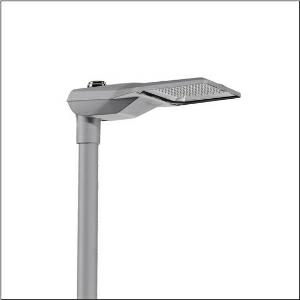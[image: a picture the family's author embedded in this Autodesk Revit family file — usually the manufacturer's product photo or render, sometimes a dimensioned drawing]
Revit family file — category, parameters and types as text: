
# Revit family: streetlight_sl_21_midi___p0_8a_5xe7u57n08mb_b7af
name_source: partatom
category: Lighting Fixtures
units: mm (PartAtom-declared; Revit-internal decimal feet)

## family parameters
Cut with Voids When Loaded = No
Host = Face
Light Source = No
Part Type = Normal
Room Calculation Point = No
Round Connector Dimension = Use Diameter
Shared = No

## types (1)
- --- (1 x LED, 15940 lm, 137 W, 3000K)
    Apparent Load = 137 VA
    CIE Flux Codes = 33 69 96 100 100
    Color Rendering = 80
    Color Temperature = 3000K
    Default Elevation = 1800 mm
    Description = Streetlight SL 21 midi, mast luminaire, primary light control with lens, of PMMA, primary optical cover: cover, of toughened safety glass, transparent, light distribution: P0.8a, light emission: direct distribution, primary light characteristic: asymmetric, installation type: side-entry, LED, 3G 2.5mm², High Power LED, rated luminous flux: 15.940lm, luminous efficacy: 116lm/W, light colour: 830, colour temperature: 3000K, control gear: NEMA (7pin), control: flexible luminous flux parameterisation, time-dependent luminous flux control, constant luminous flux control, pre-setting: linear dimming characteristic, overheat protection, mains connection: 220..240V, AC, 50/60Hz, connection cable pre-assembled, cable length: 12,5m, wiring characteristics: H05VV-F, start of lifetime: 137W, end of service life: 144W, reduction: 61W, luminaire housing, of diecast aluminium (EN AC-44300), powder-coated, Siteco® metallic grey (DB 702S), corrosivity category C5 mid according to DIN EN ISO 12944, multi-level sealing system, sealing non-destructively replaceable, inclination adjustable: 0°, 5°, 10°, 15°, length: 644mm, width: 335mm, height: 110mm, spigot size: 42mm (side-entry), mounting height: 4..8m, protection rating (complete): IP66, insulation class (complete): insulation class I (protective earthing), certification: CE, ENEC, ENEC+, VDE, impact resistance: IK10, permissible operating ambient temperature for outdoor applications: -40..+50°C, standard-compliant lighting for roads and squares, packaging unit: 1 piece

Light Distribution: P0.8a
    Height = 111 mm
    Lamp = 1 x LED
    Lamp Light Flux = 15940 lm
    Lamp Power = 137 W
    Lamp count = 1
    Length = 644 mm
    Luminous efficacy = 116 lm/W
    Manufacturer = Siteco
    ModVariant = No
    Model = 5XE7U57N08MB
    Number of Poles = 1
    OnlyDefault = Yes
    Power Factor = 1
    Product Name = Streetlight SL 21 midi | P0.8a
    Product group = mast luminaire | pylon top
    ProductGroupID = 6100
    Protection Class = Protection class I
    Protection Degree = IP 66
    RLX_Detail_Level = 1
    RLX_Emergency_Light_Flux = 0 lm
    RLX_Emergency_Type = 0
    RLX_Emergency_Type_DB = No
    RlxData = <blob elided: 90361 chars, md5=3e0dea21>
    Socket = socket
    Standby Power = 0 W
    System Light Flux = 15940 lm
    System Power = 137 W
    Type Comments = factory setting: luminous flux: 100 % | dim-lin: 254 | 700 mA
    Type Image = l_1294377.jpg
    URL = http://relux.com
    VarID = @adj_094753
    Voltage = 0 V
    Weight = 0.00 kg
    Width = 336 mm

## geometry (parser evidence)
native form markers: Blend x4, Sweep x13
no freeform markers — native parametric forms only
